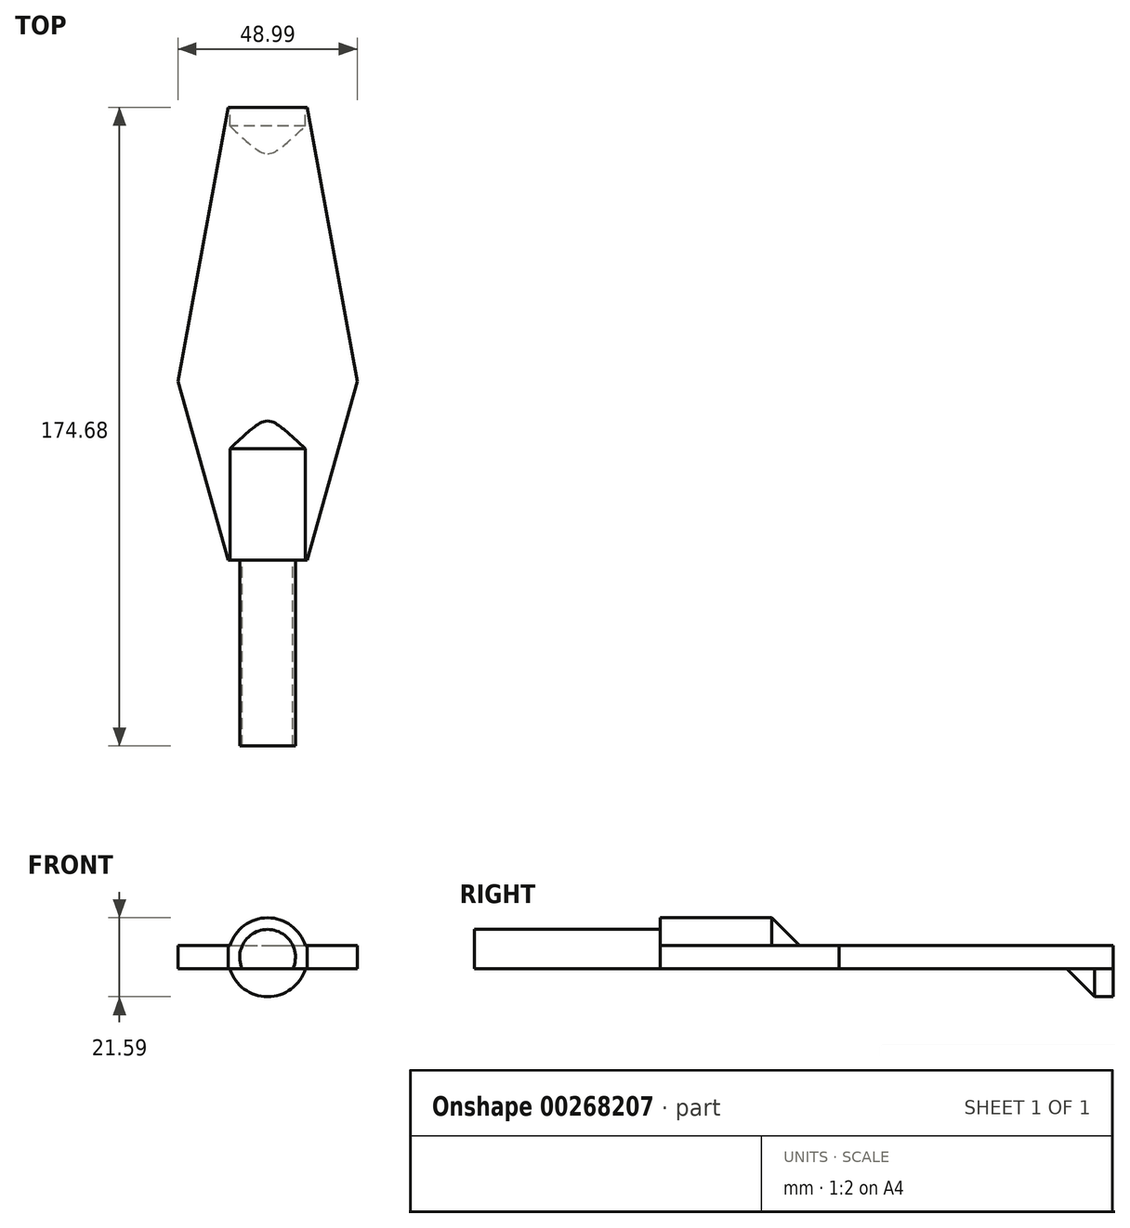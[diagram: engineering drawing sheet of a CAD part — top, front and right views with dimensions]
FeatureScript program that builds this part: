
annotation { "Feature Type Name" : "Feature", "Feature Type Description" : "" }
export const myFeature = defineFeature(function(context is Context, id is Id, definition is map)
    precondition{}
    {
        {
            var Q0;
            Q0=qCreatedBy(makeId("Top.planeOp"),FACE);
            var sketch = newSketch(context, id + "F0", { "sketchPlane" : qUnion([Q0])});
            skLineSegment(sketch, "E0", {"start": v(0, 0) * mm, "end": v(-13.7, 48.92) * mm});
            skLineSegment(sketch, "E1", {"start": v(-13.7, 48.92) * mm, "end": v(0, 123.88) * mm});
            skLineSegment(sketch, "E2", {"start": v(0, 123.88) * mm, "end": v(21.59, 123.88) * mm});
            skLineSegment(sketch, "E3", {"start": v(21.59, 123.88) * mm, "end": v(35.3, 48.92) * mm});
            skLineSegment(sketch, "E4", {"start": v(35.3, 48.92) * mm, "end": v(21.59, 0) * mm});
            skLineSegment(sketch, "E5", {"start": v(21.59, 0) * mm, "end": v(0, 0) * mm});
            skSolve(sketch);
        }
        {
            var Q0;
            Q0=makeQuery(id+"F0.imprint","IMPRINT",FACE,{"disambiguationData":[TD([[makeQuery(id+"F0.imprint","IMPRINT",EDGE,{"derivedFrom":sQuery(id+"F0.wireOp",EDGE,"E0")}),-1.0]])]});
            extrude(context, id + "F1", {"entities" : qUnion([Q0]), "depth" : 6.35 * mm});
        }
        {
            var Q0;
            Q0=makeQuery(id+"F1.opExtrude","SWEPT_FACE",FACE,{"disambiguationData":[OSD([sQuery(id+"F0.wireOp",EDGE,"E5")])]});
            var sketch = newSketch(context, id + "F2", { "sketchPlane" : qUnion([Q0])});
            skLineSegment(sketch, "E6", {"start": v(10.8, 0) * mm, "end": v(10.8, 6.35) * mm, "construction": true});
            skCircle(sketch, "E7", {"center": v(10.8, 3.18) * mm, "radius": 10.8 * mm});
            skCircle(sketch, "E8", {"center": v(10.8, 3.18) * mm, "radius": 7.62 * mm});
            skSolve(sketch);
        }
        {
            var Q0;
            {var subQ0=sQuery(id+"F2.wireOp",EDGE,"E7");var subQ1=makeQuery(id+"F1.opExtrude","CAP_EDGE",EDGE,{"disambiguationData":[OSD([sQuery(id+"F0.wireOp",EDGE,"E5")])],"isStart":true});var subQ2=makeQuery(id+"F2.imprint","INTERSECT",VERTEX,{"disambiguationData":[OD(0.0)],"derivedFrom":[subQ1,subQ0]});Q0=makeQuery(id+"F2.imprint","IMPRINT",FACE,{"disambiguationData":[TD([[makeQuery(id+"F2.imprint","IMPRINT",EDGE,{"disambiguationData":[TD([[subQ2,-1.0]])],"derivedFrom":subQ0}),1.0]])]});}
            var Q1;
            {var subQ1=sQuery(id+"F0.wireOp",EDGE,"E5");var subQ4=sQuery(id+"F2.wireOp",EDGE,"E8");var subQ7=makeQuery(id+"F1.opExtrude","CAP_EDGE",EDGE,{"disambiguationData":[OSD([subQ1])],"isStart":false});var subQ8=makeQuery(id+"F2.imprint","INTERSECT",VERTEX,{"disambiguationData":[OD(1.0)],"derivedFrom":[subQ7,subQ4]});Q1=makeQuery(id+"F2.imprint","IMPRINT",FACE,{"disambiguationData":[TD([[makeQuery(id+"F2.imprint","IMPRINT",EDGE,{"disambiguationData":[TD([[subQ8,1.0]])],"derivedFrom":subQ4}),-1.0]])]});}
            var Q2;
            {var subQ0=sQuery(id+"F2.wireOp",EDGE,"E8");var subQ1=sQuery(id+"F0.wireOp",EDGE,"E5");var subQ2=makeQuery(id+"F1.opExtrude","CAP_EDGE",EDGE,{"disambiguationData":[OSD([subQ1])],"isStart":false});var subQ3=makeQuery(id+"F2.imprint","INTERSECT",VERTEX,{"disambiguationData":[OD(0.0)],"derivedFrom":[subQ2,subQ0]});Q2=makeQuery(id+"F2.imprint","IMPRINT",FACE,{"disambiguationData":[TD([[makeQuery(id+"F2.imprint","IMPRINT",EDGE,{"disambiguationData":[TD([[subQ3,-1.0]])],"derivedFrom":subQ0}),-1.0]])]});}
            var Q3;
            {var subQ0=sQuery(id+"F2.wireOp",EDGE,"E8");var subQ1=makeQuery(id+"F1.opExtrude","CAP_EDGE",EDGE,{"disambiguationData":[OSD([sQuery(id+"F0.wireOp",EDGE,"E5")])],"isStart":false});var subQ2=makeQuery(id+"F2.imprint","INTERSECT",VERTEX,{"disambiguationData":[OD(0.0)],"derivedFrom":[subQ1,subQ0]});Q3=makeQuery(id+"F2.imprint","IMPRINT",FACE,{"disambiguationData":[TD([[makeQuery(id+"F2.imprint","IMPRINT",EDGE,{"disambiguationData":[TD([[subQ2,1.0]])],"derivedFrom":subQ0}),1.0]])]});}
            var Q4;
            {var subQ0=sQuery(id+"F2.wireOp",EDGE,"E7");var subQ1=makeQuery(id+"F1.opExtrude","CAP_EDGE",EDGE,{"disambiguationData":[OSD([sQuery(id+"F0.wireOp",EDGE,"E5")])],"isStart":false});var subQ2=makeQuery(id+"F2.imprint","INTERSECT",VERTEX,{"disambiguationData":[OD(0.0)],"derivedFrom":[subQ1,subQ0]});Q4=makeQuery(id+"F2.imprint","IMPRINT",FACE,{"disambiguationData":[TD([[makeQuery(id+"F2.imprint","IMPRINT",EDGE,{"disambiguationData":[TD([[subQ2,-1.0]])],"derivedFrom":subQ0}),1.0]])]});}
            var Q5;
            {var subQ0=sQuery(id+"F2.wireOp",EDGE,"E8");var subQ1=sQuery(id+"F0.wireOp",EDGE,"E5");var subQ2=makeQuery(id+"F1.opExtrude","CAP_EDGE",EDGE,{"disambiguationData":[OSD([subQ1])],"isStart":false});var subQ3=makeQuery(id+"F2.imprint","INTERSECT",VERTEX,{"disambiguationData":[OD(0.0)],"derivedFrom":[subQ2,subQ0]});Q5=makeQuery(id+"F2.imprint","IMPRINT",FACE,{"disambiguationData":[TD([[makeQuery(id+"F2.imprint","IMPRINT",EDGE,{"disambiguationData":[TD([[subQ3,-1.0]])],"derivedFrom":subQ0}),1.0]])]});}
            var Q6;
            {var subQ0=sQuery(id+"F2.wireOp",EDGE,"E8");var subQ1=makeQuery(id+"F1.opExtrude","CAP_EDGE",EDGE,{"disambiguationData":[OSD([sQuery(id+"F0.wireOp",EDGE,"E5")])],"isStart":true});var subQ2=makeQuery(id+"F2.imprint","INTERSECT",VERTEX,{"disambiguationData":[OD(0.0)],"derivedFrom":[subQ1,subQ0]});Q6=makeQuery(id+"F2.imprint","IMPRINT",FACE,{"disambiguationData":[TD([[makeQuery(id+"F2.imprint","IMPRINT",EDGE,{"disambiguationData":[TD([[subQ2,-1.0]])],"derivedFrom":subQ0}),1.0]])]});}
            extrude(context, id + "F3", {"entities" : qUnion([Q0, Q1, Q2, Q3, Q4, Q5, Q6]), "operationType" : NewBodyOperationType.ADD, "oppositeDirection" : true, "depth" : 38.1 * mm});
        }
        {
            var Q0;
            {var subQ0=sQuery(id+"F2.wireOp",EDGE,"E8");var subQ1=makeQuery(id+"F1.opExtrude","CAP_EDGE",EDGE,{"disambiguationData":[OSD([sQuery(id+"F0.wireOp",EDGE,"E5")])],"isStart":false});var subQ2=makeQuery(id+"F2.imprint","INTERSECT",VERTEX,{"disambiguationData":[OD(0.0)],"derivedFrom":[subQ1,subQ0]});Q0=makeQuery(id+"F2.imprint","IMPRINT",FACE,{"disambiguationData":[TD([[makeQuery(id+"F2.imprint","IMPRINT",EDGE,{"disambiguationData":[TD([[subQ2,1.0]])],"derivedFrom":subQ0}),1.0]])]});}
            var Q1;
            {var subQ0=sQuery(id+"F2.wireOp",EDGE,"E8");var subQ1=sQuery(id+"F0.wireOp",EDGE,"E5");var subQ2=makeQuery(id+"F1.opExtrude","CAP_EDGE",EDGE,{"disambiguationData":[OSD([subQ1])],"isStart":false});var subQ3=makeQuery(id+"F2.imprint","INTERSECT",VERTEX,{"disambiguationData":[OD(0.0)],"derivedFrom":[subQ2,subQ0]});Q1=makeQuery(id+"F2.imprint","IMPRINT",FACE,{"disambiguationData":[TD([[makeQuery(id+"F2.imprint","IMPRINT",EDGE,{"disambiguationData":[TD([[subQ3,-1.0]])],"derivedFrom":subQ0}),1.0]])]});}
            var Q2;
            {var subQ0=sQuery(id+"F2.wireOp",EDGE,"E8");var subQ1=makeQuery(id+"F1.opExtrude","CAP_EDGE",EDGE,{"disambiguationData":[OSD([sQuery(id+"F0.wireOp",EDGE,"E5")])],"isStart":true});var subQ2=makeQuery(id+"F2.imprint","INTERSECT",VERTEX,{"disambiguationData":[OD(0.0)],"derivedFrom":[subQ1,subQ0]});Q2=makeQuery(id+"F2.imprint","IMPRINT",FACE,{"disambiguationData":[TD([[makeQuery(id+"F2.imprint","IMPRINT",EDGE,{"disambiguationData":[TD([[subQ2,-1.0]])],"derivedFrom":subQ0}),1.0]])]});}
            extrude(context, id + "F4", {"entities" : qUnion([Q0, Q1, Q2]), "operationType" : NewBodyOperationType.ADD, "depth" : 50.8 * mm});
        }
        {
            var Q0;
            Q0=makeQuery(id+"F1.opExtrude","SWEPT_FACE",FACE,{"disambiguationData":[OSD([sQuery(id+"F0.wireOp",EDGE,"E2")])]});
            var sketch = newSketch(context, id + "F5", { "sketchPlane" : qUnion([Q0])});
            skCircle(sketch, "E9", {"center": v(-10.8, 3.18) * mm, "radius": 10.8 * mm});
            skPoint(sketch, "E9.centerSnap0", {"position": v(-10.8, 0) * mm});
            skPoint(sketch, "E9.centerSnap1", {"position": v(-21.59, 3.18) * mm});
            skSolve(sketch);
        }
        {
            var Q0;
            {var subQ0=sQuery(id+"F5.wireOp",EDGE,"E9");var subQ1=makeQuery(id+"F1.opExtrude","CAP_EDGE",EDGE,{"disambiguationData":[OSD([sQuery(id+"F0.wireOp",EDGE,"E2")])],"isStart":false});var subQ2=makeQuery(id+"F5.imprint","INTERSECT",VERTEX,{"disambiguationData":[OD(0.0)],"derivedFrom":[subQ1,subQ0]});Q0=makeQuery(id+"F5.imprint","IMPRINT",FACE,{"disambiguationData":[TD([[makeQuery(id+"F5.imprint","IMPRINT",EDGE,{"disambiguationData":[TD([[subQ2,-1.0]])],"derivedFrom":subQ0}),1.0]])]});}
            var Q1;
            {var subQ0=sQuery(id+"F5.wireOp",EDGE,"E9");var subQ1=makeQuery(id+"F1.opExtrude","CAP_EDGE",EDGE,{"disambiguationData":[OSD([sQuery(id+"F0.wireOp",EDGE,"E2")])],"isStart":true});var subQ2=makeQuery(id+"F5.imprint","INTERSECT",VERTEX,{"disambiguationData":[OD(0.0)],"derivedFrom":[subQ1,subQ0]});Q1=makeQuery(id+"F5.imprint","IMPRINT",FACE,{"disambiguationData":[TD([[makeQuery(id+"F5.imprint","IMPRINT",EDGE,{"disambiguationData":[TD([[subQ2,-1.0]])],"derivedFrom":subQ0}),1.0]])]});}
            extrude(context, id + "F6", {"entities" : qUnion([Q0, Q1]), "operationType" : NewBodyOperationType.ADD, "oppositeDirection" : true, "depth" : 12.7 * mm});
        }
        {
            var Q0;
            {var subQ0=sQuery(id+"F2.wireOp",EDGE,"E7");Q0=makeQuery(id+"F3.boolean.opBoolean","SPLIT",EDGE,{"disambiguationData":[TD([makeQuery(id+"F1.opExtrude","CAP_FACE",FACE,{"disambiguationData":[OSD([sQuery(id+"F0.wireOp",EDGE,"E0"),sQuery(id+"F0.wireOp",EDGE,"E1"),sQuery(id+"F0.wireOp",EDGE,"E2"),sQuery(id+"F0.wireOp",EDGE,"E3"),sQuery(id+"F0.wireOp",EDGE,"E4"),sQuery(id+"F0.wireOp",EDGE,"E5")])],"isStart":false})])],"derivedFrom":makeQuery(id+"F3.opExtrude","CAP_EDGE",EDGE,{"disambiguationData":[OSD([subQ0])],"isStart":false})});}
            var Q1;
            {var subQ0=sQuery(id+"F2.wireOp",EDGE,"E7");Q1=makeQuery(id+"F3.boolean.opBoolean","SPLIT",EDGE,{"disambiguationData":[TD([makeQuery(id+"F1.opExtrude","CAP_FACE",FACE,{"disambiguationData":[OSD([sQuery(id+"F0.wireOp",EDGE,"E0"),sQuery(id+"F0.wireOp",EDGE,"E1"),sQuery(id+"F0.wireOp",EDGE,"E2"),sQuery(id+"F0.wireOp",EDGE,"E3"),sQuery(id+"F0.wireOp",EDGE,"E4"),sQuery(id+"F0.wireOp",EDGE,"E5")])],"isStart":true})])],"derivedFrom":makeQuery(id+"F3.opExtrude","CAP_EDGE",EDGE,{"disambiguationData":[OSD([subQ0])],"isStart":false})});}
            var Q2;
            {var subQ0=sQuery(id+"F5.wireOp",EDGE,"E9");var subQ1=makeQuery(id+"F1.opExtrude","CAP_EDGE",EDGE,{"disambiguationData":[OSD([sQuery(id+"F0.wireOp",EDGE,"E2")])],"isStart":false});Q2=makeQuery(id+"F6.opExtrude","CAP_EDGE",EDGE,{"disambiguationData":[OSD([subQ0]),TDD([makeQuery(id+"F5.imprint","IMPRINT",EDGE,{"disambiguationData":[TD([[makeQuery(id+"F5.imprint","INTERSECT",VERTEX,{"disambiguationData":[OD(0.0)],"derivedFrom":[subQ1,subQ0]}),-1.0]])],"derivedFrom":subQ0})])],"isStart":false});}
            var Q3;
            {var subQ0=sQuery(id+"F5.wireOp",EDGE,"E9");var subQ1=makeQuery(id+"F1.opExtrude","CAP_EDGE",EDGE,{"disambiguationData":[OSD([sQuery(id+"F0.wireOp",EDGE,"E2")])],"isStart":true});Q3=makeQuery(id+"F6.opExtrude","CAP_EDGE",EDGE,{"disambiguationData":[OSD([subQ0]),TDD([makeQuery(id+"F5.imprint","IMPRINT",EDGE,{"disambiguationData":[TD([[makeQuery(id+"F5.imprint","INTERSECT",VERTEX,{"disambiguationData":[OD(0.0)],"derivedFrom":[subQ1,subQ0]}),-1.0]])],"derivedFrom":subQ0})])],"isStart":false});}
            chamfer(context, id + "F7", {"entities" : qUnion([Q0, Q1, Q2, Q3]), "width" : 7.62 * mm, "tangentPropagation" : true});
        }
    });
